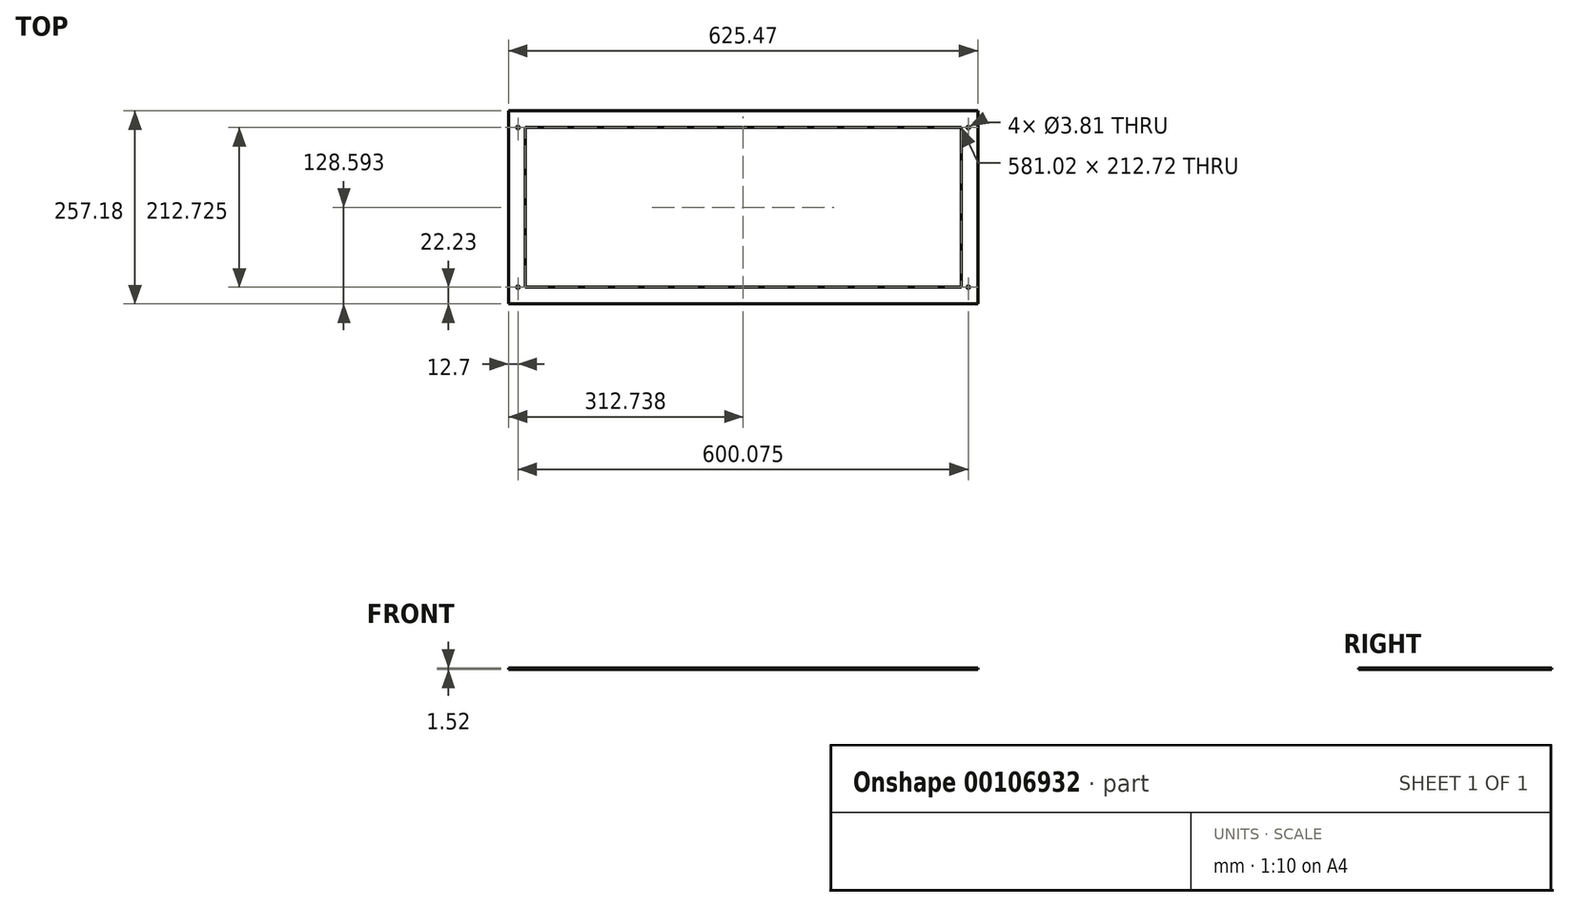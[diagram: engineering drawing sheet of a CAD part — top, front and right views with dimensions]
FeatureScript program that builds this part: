
annotation { "Feature Type Name" : "Feature", "Feature Type Description" : "" }
export const myFeature = defineFeature(function(context is Context, id is Id, definition is map)
    precondition{}
    {
        {
            var Q0;
            Q0=qCreatedBy(makeId("Top.planeOp"),FACE);
            var sketch = newSketch(context, id + "F0", { "sketchPlane" : qUnion([Q0])});
            skLineSegment(sketch, "E0", {"start": v(0, 0) * mm, "end": v(0, 212.73) * mm, "construction": true});
            skLineSegment(sketch, "E1", {"start": v(0, 0) * mm, "end": v(600.08, 0) * mm, "construction": true});
            skLineSegment(sketch, "E2", {"start": v(0, 212.73) * mm, "end": v(600.08, 212.73) * mm, "construction": true});
            skLineSegment(sketch, "E3", {"start": v(600.08, 212.73) * mm, "end": v(600.08, 0) * mm, "construction": true});
            skCircle(sketch, "E4", {"center": v(600.08, 212.73) * mm, "radius": 1.9 * mm});
            skCircle(sketch, "E5", {"center": v(600.08, 0) * mm, "radius": 1.9 * mm});
            skCircle(sketch, "E6", {"center": v(0, 0) * mm, "radius": 1.9 * mm});
            skCircle(sketch, "E7", {"center": v(0, 212.73) * mm, "radius": 1.9 * mm});
            skLineSegment(sketch, "E8.bottom", {"start": v(-12.7, 234.95) * mm, "end": v(612.78, 234.95) * mm});
            skLineSegment(sketch, "E8.top", {"start": v(-12.7, -22.23) * mm, "end": v(612.78, -22.23) * mm});
            skLineSegment(sketch, "E8.left", {"start": v(-12.7, 234.95) * mm, "end": v(-12.7, -22.22) * mm});
            skLineSegment(sketch, "E8.right", {"start": v(612.78, 234.95) * mm, "end": v(612.78, -22.22) * mm});
            skLineSegment(sketch, "E9", {"start": v(9.52, 212.73) * mm, "end": v(9.53, 0) * mm, "construction": true});
            skLineSegment(sketch, "E10", {"start": v(590.55, 212.73) * mm, "end": v(590.55, 0) * mm, "construction": true});
            skLineSegment(sketch, "E11.bottom", {"start": v(9.53, 212.73) * mm, "end": v(590.55, 212.73) * mm});
            skLineSegment(sketch, "E11.top", {"start": v(9.53, 0) * mm, "end": v(590.55, 0) * mm});
            skLineSegment(sketch, "E11.left", {"start": v(9.52, 212.73) * mm, "end": v(9.52, 0) * mm});
            skLineSegment(sketch, "E11.right", {"start": v(590.55, 212.73) * mm, "end": v(590.55, 0) * mm});
            skSolve(sketch);
        }
        {
            var Q0;
            Q0=makeQuery(id+"F0.imprint","IMPRINT",FACE,{"disambiguationData":[TD([[makeQuery(id+"F0.imprint","IMPRINT",EDGE,{"derivedFrom":sQuery(id+"F0.wireOp",EDGE,"E4")}),-1.0]])]});
            extrude(context, id + "F1", {"entities" : qUnion([Q0]), "depth" : 1.52 * mm});
        }
    });
